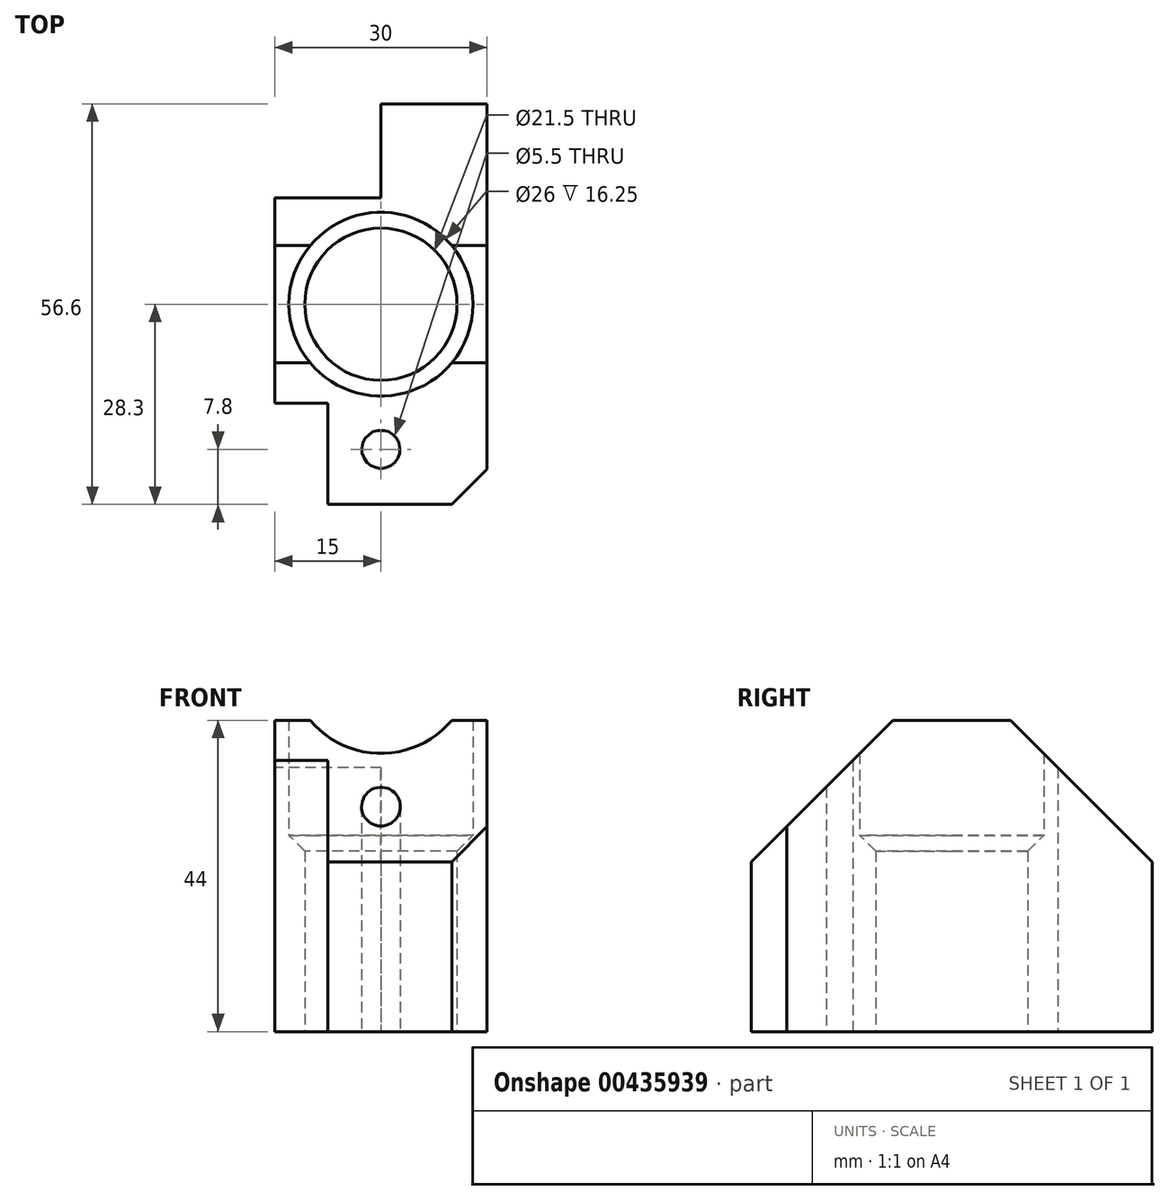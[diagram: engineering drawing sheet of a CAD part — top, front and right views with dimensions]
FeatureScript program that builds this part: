
annotation { "Feature Type Name" : "Feature", "Feature Type Description" : "" }
export const myFeature = defineFeature(function(context is Context, id is Id, definition is map)
    precondition{}
    {
        {
            var Q0;
            Q0=qCreatedBy(makeId("Top.planeOp"),FACE);
            var sketch = newSketch(context, id + "F0", { "sketchPlane" : qUnion([Q0])});
            skCircle(sketch, "E0", {"center": v(0, 0) * mm, "radius": 10.75 * mm});
            skCircle(sketch, "E1", {"center": v(0, -20.5) * mm, "radius": 2.75 * mm});
            skLineSegment(sketch, "E2", {"start": v(0, 15) * mm, "end": v(-15, 15) * mm});
            skLineSegment(sketch, "E3", {"start": v(-15, 15) * mm, "end": v(-15, -14) * mm});
            skLineSegment(sketch, "E4", {"start": v(-7.5, -28.3) * mm, "end": v(0, -28.3) * mm});
            skLineSegment(sketch, "E5", {"start": v(0, 15) * mm, "end": v(0, -28.3) * mm, "construction": true});
            skLineSegment(sketch, "E6.MirrorCS", {"start": v(15, -28.3) * mm, "end": v(0, -28.3) * mm});
            skLineSegment(sketch, "E7.MirrorCS", {"start": v(15, 15) * mm, "end": v(15, -28.3) * mm});
            skLineSegment(sketch, "E8", {"start": v(0, 15) * mm, "end": v(0, 28.3) * mm});
            skLineSegment(sketch, "E9", {"start": v(0, 28.3) * mm, "end": v(15, 28.3) * mm});
            skLineSegment(sketch, "E10", {"start": v(15, 28.3) * mm, "end": v(15, 15) * mm});
            skPoint(sketch, "E11.MirrorCS.start.orphan", {"position": v(0, 15) * mm});
            skPoint(sketch, "E12", {"position": v(-7.5, -28.3) * mm});
            skPoint(sketch, "E13", {"position": v(-15, 0) * mm});
            skLineSegment(sketch, "E14", {"start": v(-7.5, -28.3) * mm, "end": v(-7.5, -14) * mm});
            skLineSegment(sketch, "E15", {"start": v(-7.5, -14) * mm, "end": v(-15, -14) * mm});
            skPoint(sketch, "E16.orphan", {"position": v(-15, -28.3) * mm});
            skCircle(sketch, "E17", {"center": v(0, 0) * mm, "radius": 13 * mm});
            skSolve(sketch);
        }
        {
            var Q0;
            Q0=makeQuery(id+"F0.imprint","IMPRINT",FACE,{"disambiguationData":[TD([[makeQuery(id+"F0.imprint","IMPRINT",EDGE,{"derivedFrom":sQuery(id+"F0.wireOp",EDGE,"E0")}),-1.0]])]});
            var Q1;
            Q1=makeQuery(id+"F0.imprint","IMPRINT",FACE,{"disambiguationData":[TD([[makeQuery(id+"F0.imprint","IMPRINT",EDGE,{"derivedFrom":sQuery(id+"F0.wireOp",EDGE,"E1")}),-1.0]])]});
            extrude(context, id + "F1", {"entities" : qUnion([Q0, Q1]), "depth" : 30 * mm});
        }
        {
            var Q0;
            Q0=makeQuery(id+"F0.imprint","IMPRINT",FACE,{"disambiguationData":[TD([[makeQuery(id+"F0.imprint","IMPRINT",EDGE,{"derivedFrom":sQuery(id+"F0.wireOp",EDGE,"E1")}),-1.0]])]});
            extrude(context, id + "F2", {"entities" : qUnion([Q0]), "operationType" : NewBodyOperationType.ADD, "depth" : 44 * mm, "hasSecondDirection" : true, "secondDirectionOppositeDirection" : false, "secondDirectionDepth" : 30 * mm});
        }
        {
            var Q0;
            Q0=makeQuery(id+"F1.opExtrude","CAP_EDGE",EDGE,{"disambiguationData":[OSD([sQuery(id+"F0.wireOp",EDGE,"E0")])],"isStart":false});
            chamfer(context, id + "F3", {"entities" : qUnion([Q0]), "width" : 4.5 * mm, "tangentPropagation" : true});
        }
        {
            var Q0;
            {var subQ0=sQuery(id+"F0.wireOp",EDGE,"E7.MirrorCS");var subQ1=sQuery(id+"F0.wireOp",EDGE,"E6.MirrorCS");Q0=makeQuery(id+"F2.boolean.opBoolean","MERGE",EDGE,{"derivedFrom":[makeQuery(id+"F1.opExtrude","SWEPT_EDGE",EDGE,{"disambiguationData":[OSD([subQ1,subQ0])]}),makeQuery(id+"F2.opExtrude","SWEPT_EDGE",EDGE,{"disambiguationData":[OSD([subQ1,subQ0])]})]});}
            chamfer(context, id + "F4", {"entities" : qUnion([Q0]), "width" : 5 * mm, "tangentPropagation" : true});
        }
        {
            var Q0;
            Q0=makeQuery(id+"F2.opExtrude","CAP_EDGE",EDGE,{"disambiguationData":[OSD([sQuery(id+"F0.wireOp",EDGE,"E9")])],"isStart":false});
            var Q1;
            Q1=makeQuery(id+"F2.opExtrude","CAP_EDGE",EDGE,{"disambiguationData":[OSD([sQuery(id+"F0.wireOp",EDGE,"E4"),sQuery(id+"F0.wireOp",EDGE,"E6.MirrorCS")])],"isStart":false});
            chamfer(context, id + "F5", {"entities" : qUnion([Q0, Q1]), "width" : 20 * mm, "tangentPropagation" : true});
        }
    });
